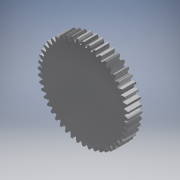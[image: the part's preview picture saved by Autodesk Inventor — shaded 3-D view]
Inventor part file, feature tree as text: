
AUTODESK INVENTOR PART (.ipt)
format: ipt  version: 2019 (Build 230136000, 136)  size: 327,168 bytes
history: native  units: mm (DEFAULTED — no unit token found)
features: plane x3, other x3, sketch x2, extrude x1
ambient origin geometry x8: Origin, YZ Plane, XZ Plane, XY Plane, X Axis, Y Axis, Z Axis, Center Point
bodies: Solid1 (feature_tree)
feature tree (9):
  extrude  "Extrusion1"  Depth=1.5mm TaperAngle=0.0deg
  plane  "Work Plane2"
  plane  "Work Plane8"
  plane  "Work Plane9"
  other  "Spur Gear"
  sketch  "Sketch1"  dims[d0=9.95mm d1=1.5mm d2=0.0mm]
  sketch  "Sketch2"  dims[d3=9.56mm d4=10.0mm d5=0.0mm d16=5.975mm d17=0.0mm d34=0.654498mm d39=0.0mm d41=0.0mm d43=5.975mm d46=5.975mm d47=0.0mm d48=0.0mm]
  other  "Srf1"
  other  "Pitch Diameter"
